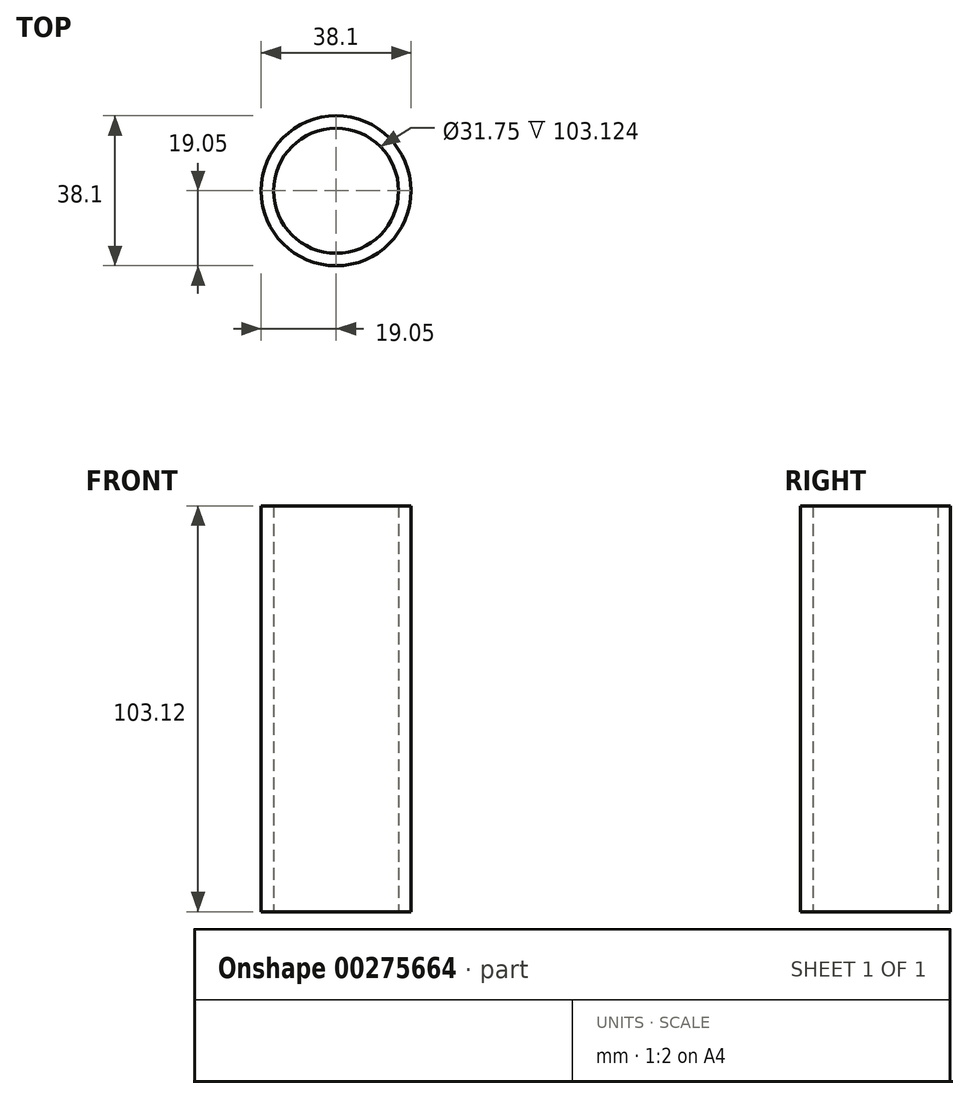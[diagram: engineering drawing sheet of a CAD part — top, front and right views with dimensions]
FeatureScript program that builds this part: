
annotation { "Feature Type Name" : "Feature", "Feature Type Description" : "" }
export const myFeature = defineFeature(function(context is Context, id is Id, definition is map)
    precondition{}
    {
        {
            var Q0;
            Q0=qCreatedBy(makeId("Top.planeOp"),FACE);
            var sketch = newSketch(context, id + "F0", { "sketchPlane" : qUnion([Q0])});
            skCircle(sketch, "E0", {"center": v(0, 0) * mm, "radius": 15.88 * mm});
            skCircle(sketch, "E1", {"center": v(0, 0) * mm, "radius": 19.05 * mm});
            skSolve(sketch);
        }
        {
            var Q0;
            Q0 = qSketchRegion(id + "F0", true);
            extrude(context, id + "F1", {"entities" : qUnion([Q0]), "depth" : 103.12 * mm});
        }
    });
